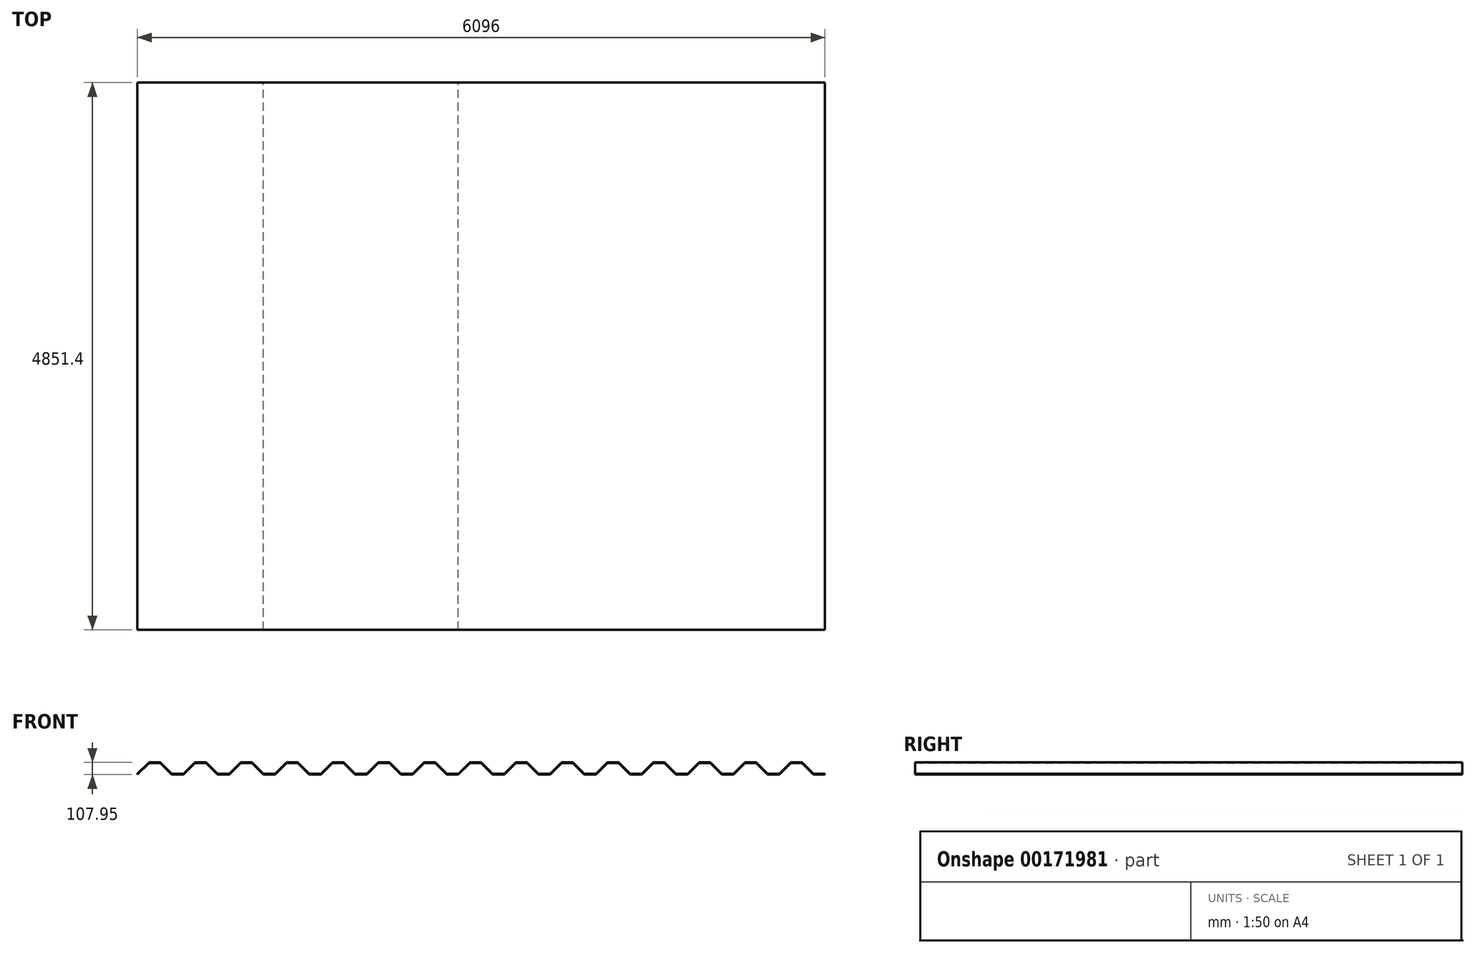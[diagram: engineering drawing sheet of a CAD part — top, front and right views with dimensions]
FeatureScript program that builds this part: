
annotation { "Feature Type Name" : "Feature", "Feature Type Description" : "" }
export const myFeature = defineFeature(function(context is Context, id is Id, definition is map)
    precondition{}
    {
        {
            var Q0;
            Q0=qCreatedBy(makeId("Front.planeOp"),FACE);
            var sketch = newSketch(context, id + "F0", { "sketchPlane" : qUnion([Q0])});
            skLineSegment(sketch, "E0", {"start": v(0, 0) * mm, "end": v(101.6, 101.6) * mm});
            skLineSegment(sketch, "E1", {"start": v(101.6, 101.6) * mm, "end": v(203.2, 101.6) * mm});
            skLineSegment(sketch, "E2", {"start": v(203.2, 101.6) * mm, "end": v(304.8, 0) * mm});
            skLineSegment(sketch, "E3", {"start": v(304.8, 0) * mm, "end": v(406.4, 0) * mm});
            skLineSegment(sketch, "E4.1.0.0", {"start": v(406.4, 0) * mm, "end": v(508, 101.6) * mm});
            skLineSegment(sketch, "E4.1.0.1", {"start": v(508, 101.6) * mm, "end": v(609.6, 101.6) * mm});
            skLineSegment(sketch, "E4.1.0.2", {"start": v(609.6, 101.6) * mm, "end": v(711.2, 0) * mm});
            skLineSegment(sketch, "E4.1.0.3", {"start": v(711.2, 0) * mm, "end": v(812.8, 0) * mm});
            skLineSegment(sketch, "E4.2.0.0", {"start": v(812.8, 0) * mm, "end": v(914.4, 101.6) * mm});
            skLineSegment(sketch, "E4.2.0.1", {"start": v(914.4, 101.6) * mm, "end": v(1016, 101.6) * mm});
            skLineSegment(sketch, "E4.2.0.2", {"start": v(1016, 101.6) * mm, "end": v(1117.6, 0) * mm});
            skLineSegment(sketch, "E4.2.0.3", {"start": v(1117.6, 0) * mm, "end": v(1219.2, 0) * mm});
            skLineSegment(sketch, "E4.3.0.0", {"start": v(1219.2, 0) * mm, "end": v(1320.8, 101.6) * mm});
            skLineSegment(sketch, "E4.3.0.1", {"start": v(1320.8, 101.6) * mm, "end": v(1422.4, 101.6) * mm});
            skLineSegment(sketch, "E4.3.0.2", {"start": v(1422.4, 101.6) * mm, "end": v(1524, 0) * mm});
            skLineSegment(sketch, "E4.3.0.3", {"start": v(1524, 0) * mm, "end": v(1625.6, 0) * mm});
            skLineSegment(sketch, "E4.4.0.0", {"start": v(1625.6, 0) * mm, "end": v(1727.2, 101.6) * mm});
            skLineSegment(sketch, "E4.4.0.1", {"start": v(1727.2, 101.6) * mm, "end": v(1828.8, 101.6) * mm});
            skLineSegment(sketch, "E4.4.0.2", {"start": v(1828.8, 101.6) * mm, "end": v(1930.4, 0) * mm});
            skLineSegment(sketch, "E4.4.0.3", {"start": v(1930.4, 0) * mm, "end": v(2032, 0) * mm});
            skLineSegment(sketch, "E4.5.0.0", {"start": v(2032, 0) * mm, "end": v(2133.6, 101.6) * mm});
            skLineSegment(sketch, "E4.5.0.1", {"start": v(2133.6, 101.6) * mm, "end": v(2235.2, 101.6) * mm});
            skLineSegment(sketch, "E4.5.0.2", {"start": v(2235.2, 101.6) * mm, "end": v(2336.8, 0) * mm});
            skLineSegment(sketch, "E4.5.0.3", {"start": v(2336.8, 0) * mm, "end": v(2438.4, 0) * mm});
            skLineSegment(sketch, "E4.6.0.0", {"start": v(2438.4, 0) * mm, "end": v(2540, 101.6) * mm});
            skLineSegment(sketch, "E4.6.0.1", {"start": v(2540, 101.6) * mm, "end": v(2641.6, 101.6) * mm});
            skLineSegment(sketch, "E4.6.0.2", {"start": v(2641.6, 101.6) * mm, "end": v(2743.2, 0) * mm});
            skLineSegment(sketch, "E4.6.0.3", {"start": v(2743.2, 0) * mm, "end": v(2844.8, 0) * mm});
            skLineSegment(sketch, "E4.7.0.0", {"start": v(2844.8, 0) * mm, "end": v(2946.4, 101.6) * mm});
            skLineSegment(sketch, "E4.7.0.1", {"start": v(2946.4, 101.6) * mm, "end": v(3048, 101.6) * mm});
            skLineSegment(sketch, "E4.7.0.2", {"start": v(3048, 101.6) * mm, "end": v(3149.6, 0) * mm});
            skLineSegment(sketch, "E4.7.0.3", {"start": v(3149.6, 0) * mm, "end": v(3251.2, 0) * mm});
            skLineSegment(sketch, "E4.8.0.0", {"start": v(3251.2, 0) * mm, "end": v(3352.8, 101.6) * mm});
            skLineSegment(sketch, "E4.8.0.1", {"start": v(3352.8, 101.6) * mm, "end": v(3454.4, 101.6) * mm});
            skLineSegment(sketch, "E4.8.0.2", {"start": v(3454.4, 101.6) * mm, "end": v(3556, 0) * mm});
            skLineSegment(sketch, "E4.8.0.3", {"start": v(3556, 0) * mm, "end": v(3657.6, 0) * mm});
            skLineSegment(sketch, "E4.9.0.0", {"start": v(3657.6, 0) * mm, "end": v(3759.2, 101.6) * mm});
            skLineSegment(sketch, "E4.9.0.1", {"start": v(3759.2, 101.6) * mm, "end": v(3860.8, 101.6) * mm});
            skLineSegment(sketch, "E4.9.0.2", {"start": v(3860.8, 101.6) * mm, "end": v(3962.4, 0) * mm});
            skLineSegment(sketch, "E4.9.0.3", {"start": v(3962.4, 0) * mm, "end": v(4064, 0) * mm});
            skLineSegment(sketch, "E4.10.0.0", {"start": v(4064, 0) * mm, "end": v(4165.6, 101.6) * mm});
            skLineSegment(sketch, "E4.10.0.1", {"start": v(4165.6, 101.6) * mm, "end": v(4267.2, 101.6) * mm});
            skLineSegment(sketch, "E4.10.0.2", {"start": v(4267.2, 101.6) * mm, "end": v(4368.8, 0) * mm});
            skLineSegment(sketch, "E4.10.0.3", {"start": v(4368.8, 0) * mm, "end": v(4470.4, 0) * mm});
            skLineSegment(sketch, "E4.11.0.0", {"start": v(4470.4, 0) * mm, "end": v(4572, 101.6) * mm});
            skLineSegment(sketch, "E4.11.0.1", {"start": v(4572, 101.6) * mm, "end": v(4673.6, 101.6) * mm});
            skLineSegment(sketch, "E4.11.0.2", {"start": v(4673.6, 101.6) * mm, "end": v(4775.2, 0) * mm});
            skLineSegment(sketch, "E4.11.0.3", {"start": v(4775.2, 0) * mm, "end": v(4876.8, 0) * mm});
            skLineSegment(sketch, "E4.12.0.0", {"start": v(4876.8, 0) * mm, "end": v(4978.4, 101.6) * mm});
            skLineSegment(sketch, "E4.12.0.1", {"start": v(4978.4, 101.6) * mm, "end": v(5080, 101.6) * mm});
            skLineSegment(sketch, "E4.12.0.2", {"start": v(5080, 101.6) * mm, "end": v(5181.6, 0) * mm});
            skLineSegment(sketch, "E4.12.0.3", {"start": v(5181.6, 0) * mm, "end": v(5283.2, 0) * mm});
            skLineSegment(sketch, "E4.13.0.0", {"start": v(5283.2, 0) * mm, "end": v(5384.8, 101.6) * mm});
            skLineSegment(sketch, "E4.13.0.1", {"start": v(5384.8, 101.6) * mm, "end": v(5486.4, 101.6) * mm});
            skLineSegment(sketch, "E4.13.0.2", {"start": v(5486.4, 101.6) * mm, "end": v(5588, 0) * mm});
            skLineSegment(sketch, "E4.13.0.3", {"start": v(5588, 0) * mm, "end": v(5689.6, 0) * mm});
            skLineSegment(sketch, "E4.14.0.0", {"start": v(5689.6, 0) * mm, "end": v(5791.2, 101.6) * mm});
            skLineSegment(sketch, "E4.14.0.1", {"start": v(5791.2, 101.6) * mm, "end": v(5892.8, 101.6) * mm});
            skLineSegment(sketch, "E4.14.0.2", {"start": v(5892.8, 101.6) * mm, "end": v(5994.4, 0) * mm});
            skLineSegment(sketch, "E4.14.0.3", {"start": v(5994.4, 0) * mm, "end": v(6096, 0) * mm});
            skLineSegment(sketch, "E5.0.1.0", {"start": v(5994.4, 6.35) * mm, "end": v(6096, 6.35) * mm});
            skLineSegment(sketch, "E5.0.1.1", {"start": v(0, 6.35) * mm, "end": v(101.6, 107.95) * mm});
            skLineSegment(sketch, "E5.0.1.2", {"start": v(5486.4, 107.95) * mm, "end": v(5588, 6.35) * mm});
            skLineSegment(sketch, "E5.0.1.3", {"start": v(5080, 107.95) * mm, "end": v(5181.6, 6.35) * mm});
            skLineSegment(sketch, "E5.0.1.4", {"start": v(2235.2, 107.95) * mm, "end": v(2336.8, 6.35) * mm});
            skLineSegment(sketch, "E5.0.1.5", {"start": v(3454.4, 107.95) * mm, "end": v(3556, 6.35) * mm});
            skLineSegment(sketch, "E5.0.1.6", {"start": v(3860.8, 107.95) * mm, "end": v(3962.4, 6.35) * mm});
            skLineSegment(sketch, "E5.0.1.7", {"start": v(1828.8, 107.95) * mm, "end": v(1930.4, 6.35) * mm});
            skLineSegment(sketch, "E5.0.1.8", {"start": v(3149.6, 6.35) * mm, "end": v(3251.2, 6.35) * mm});
            skLineSegment(sketch, "E5.0.1.9", {"start": v(4775.2, 6.35) * mm, "end": v(4876.8, 6.35) * mm});
            skLineSegment(sketch, "E5.0.1.10", {"start": v(2540, 107.95) * mm, "end": v(2641.6, 107.95) * mm});
            skLineSegment(sketch, "E5.0.1.11", {"start": v(4165.6, 107.95) * mm, "end": v(4267.2, 107.95) * mm});
            skLineSegment(sketch, "E5.0.1.12", {"start": v(5791.2, 107.95) * mm, "end": v(5892.8, 107.95) * mm});
            skLineSegment(sketch, "E5.0.1.13", {"start": v(4978.4, 107.95) * mm, "end": v(5080, 107.95) * mm});
            skLineSegment(sketch, "E5.0.1.14", {"start": v(3352.8, 107.95) * mm, "end": v(3454.4, 107.95) * mm});
            skLineSegment(sketch, "E5.0.1.15", {"start": v(1727.2, 107.95) * mm, "end": v(1828.8, 107.95) * mm});
            skLineSegment(sketch, "E5.0.1.16", {"start": v(3759.2, 107.95) * mm, "end": v(3860.8, 107.95) * mm});
            skLineSegment(sketch, "E5.0.1.17", {"start": v(3048, 107.95) * mm, "end": v(3149.6, 6.35) * mm});
            skLineSegment(sketch, "E5.0.1.18", {"start": v(4673.6, 107.95) * mm, "end": v(4775.2, 6.35) * mm});
            skLineSegment(sketch, "E5.0.1.19", {"start": v(5384.8, 107.95) * mm, "end": v(5486.4, 107.95) * mm});
            skLineSegment(sketch, "E5.0.1.20", {"start": v(2133.6, 107.95) * mm, "end": v(2235.2, 107.95) * mm});
            skLineSegment(sketch, "E5.0.1.21", {"start": v(2438.4, 6.35) * mm, "end": v(2540, 107.95) * mm});
            skLineSegment(sketch, "E5.0.1.22", {"start": v(4064, 6.35) * mm, "end": v(4165.6, 107.95) * mm});
            skLineSegment(sketch, "E5.0.1.23", {"start": v(5689.6, 6.35) * mm, "end": v(5791.2, 107.95) * mm});
            skLineSegment(sketch, "E5.0.1.24", {"start": v(2844.8, 6.35) * mm, "end": v(2946.4, 107.95) * mm});
            skLineSegment(sketch, "E5.0.1.25", {"start": v(4470.4, 6.35) * mm, "end": v(4572, 107.95) * mm});
            skLineSegment(sketch, "E5.0.1.26", {"start": v(3251.2, 6.35) * mm, "end": v(3352.8, 107.95) * mm});
            skLineSegment(sketch, "E5.0.1.27", {"start": v(4876.8, 6.35) * mm, "end": v(4978.4, 107.95) * mm});
            skLineSegment(sketch, "E5.0.1.28", {"start": v(1625.6, 6.35) * mm, "end": v(1727.2, 107.95) * mm});
            skLineSegment(sketch, "E5.0.1.29", {"start": v(3657.6, 6.35) * mm, "end": v(3759.2, 107.95) * mm});
            skLineSegment(sketch, "E5.0.1.30", {"start": v(4572, 107.95) * mm, "end": v(4673.6, 107.95) * mm});
            skLineSegment(sketch, "E5.0.1.31", {"start": v(2946.4, 107.95) * mm, "end": v(3048, 107.95) * mm});
            skLineSegment(sketch, "E5.0.1.32", {"start": v(5283.2, 6.35) * mm, "end": v(5384.8, 107.95) * mm});
            skLineSegment(sketch, "E5.0.1.33", {"start": v(2032, 6.35) * mm, "end": v(2133.6, 107.95) * mm});
            skLineSegment(sketch, "E5.0.1.34", {"start": v(2336.8, 6.35) * mm, "end": v(2438.4, 6.35) * mm});
            skLineSegment(sketch, "E5.0.1.35", {"start": v(3962.4, 6.35) * mm, "end": v(4064, 6.35) * mm});
            skLineSegment(sketch, "E5.0.1.36", {"start": v(5588, 6.35) * mm, "end": v(5689.6, 6.35) * mm});
            skLineSegment(sketch, "E5.0.1.37", {"start": v(2743.2, 6.35) * mm, "end": v(2844.8, 6.35) * mm});
            skLineSegment(sketch, "E5.0.1.38", {"start": v(4368.8, 6.35) * mm, "end": v(4470.4, 6.35) * mm});
            skLineSegment(sketch, "E5.0.1.39", {"start": v(1219.2, 6.35) * mm, "end": v(1320.8, 107.95) * mm});
            skLineSegment(sketch, "E5.0.1.40", {"start": v(1117.6, 6.35) * mm, "end": v(1219.2, 6.35) * mm});
            skLineSegment(sketch, "E5.0.1.41", {"start": v(1016, 107.95) * mm, "end": v(1117.6, 6.35) * mm});
            skLineSegment(sketch, "E5.0.1.42", {"start": v(914.4, 107.95) * mm, "end": v(1016, 107.95) * mm});
            skLineSegment(sketch, "E5.0.1.43", {"start": v(812.8, 6.35) * mm, "end": v(914.4, 107.95) * mm});
            skLineSegment(sketch, "E5.0.1.44", {"start": v(711.2, 6.35) * mm, "end": v(812.8, 6.35) * mm});
            skLineSegment(sketch, "E5.0.1.45", {"start": v(609.6, 107.95) * mm, "end": v(711.2, 6.35) * mm});
            skLineSegment(sketch, "E5.0.1.46", {"start": v(508, 107.95) * mm, "end": v(609.6, 107.95) * mm});
            skLineSegment(sketch, "E5.0.1.47", {"start": v(406.4, 6.35) * mm, "end": v(508, 107.95) * mm});
            skLineSegment(sketch, "E5.0.1.48", {"start": v(304.8, 6.35) * mm, "end": v(406.4, 6.35) * mm});
            skLineSegment(sketch, "E5.0.1.49", {"start": v(203.2, 107.95) * mm, "end": v(304.8, 6.35) * mm});
            skLineSegment(sketch, "E5.0.1.50", {"start": v(101.6, 107.95) * mm, "end": v(203.2, 107.95) * mm});
            skLineSegment(sketch, "E5.0.1.51", {"start": v(1524, 6.35) * mm, "end": v(1625.6, 6.35) * mm});
            skLineSegment(sketch, "E5.0.1.52", {"start": v(1422.4, 107.95) * mm, "end": v(1524, 6.35) * mm});
            skLineSegment(sketch, "E5.0.1.53", {"start": v(1320.8, 107.95) * mm, "end": v(1422.4, 107.95) * mm});
            skLineSegment(sketch, "E5.0.1.54", {"start": v(3556, 6.35) * mm, "end": v(3657.6, 6.35) * mm});
            skLineSegment(sketch, "E5.0.1.55", {"start": v(5181.6, 6.35) * mm, "end": v(5283.2, 6.35) * mm});
            skLineSegment(sketch, "E5.0.1.56", {"start": v(1930.4, 6.35) * mm, "end": v(2032, 6.35) * mm});
            skLineSegment(sketch, "E5.0.1.57", {"start": v(2641.6, 107.95) * mm, "end": v(2743.2, 6.35) * mm});
            skLineSegment(sketch, "E5.0.1.58", {"start": v(4267.2, 107.95) * mm, "end": v(4368.8, 6.35) * mm});
            skLineSegment(sketch, "E5.0.1.59", {"start": v(5892.8, 107.95) * mm, "end": v(5994.4, 6.35) * mm});
            skLineSegment(sketch, "E5.direction2", {"start": v(0, 0) * mm, "end": v(0, 6.35) * mm, "construction": true});
            skLineSegment(sketch, "E6", {"start": v(0, 6.35) * mm, "end": v(0, 0) * mm});
            skLineSegment(sketch, "E7", {"start": v(6096, 6.35) * mm, "end": v(6096, 0) * mm});
            skSolve(sketch);
        }
        {
            var Q0;
            Q0 = qSketchRegion(id + "F0", true);
            extrude(context, id + "F1", {"entities" : qUnion([Q0]), "depth" : 4851.4 * mm});
        }
        {
            var Q0;
            Q0=makeQuery(id+"F1.opExtrude","SWEPT_EDGE",EDGE,{"disambiguationData":[OSD([sQuery(id+"F0.wireOp",EDGE,"E5.0.1.1"),sQuery(id+"F0.wireOp",EDGE,"E5.0.1.50")])]});
            var Q1;
            Q1=makeQuery(id+"F1.opExtrude","SWEPT_EDGE",EDGE,{"disambiguationData":[OSD([sQuery(id+"F0.wireOp",EDGE,"E5.0.1.49"),sQuery(id+"F0.wireOp",EDGE,"E5.0.1.50")])]});
            var Q2;
            Q2=makeQuery(id+"F1.opExtrude","SWEPT_EDGE",EDGE,{"disambiguationData":[OSD([sQuery(id+"F0.wireOp",EDGE,"E5.0.1.48"),sQuery(id+"F0.wireOp",EDGE,"E5.0.1.49")])]});
            var Q3;
            Q3=makeQuery(id+"F1.opExtrude","SWEPT_EDGE",EDGE,{"disambiguationData":[OSD([sQuery(id+"F0.wireOp",EDGE,"E5.0.1.47"),sQuery(id+"F0.wireOp",EDGE,"E5.0.1.48")])]});
            var Q4;
            Q4=makeQuery(id+"F1.opExtrude","SWEPT_EDGE",EDGE,{"disambiguationData":[OSD([sQuery(id+"F0.wireOp",EDGE,"E5.0.1.46"),sQuery(id+"F0.wireOp",EDGE,"E5.0.1.47")])]});
            var Q5;
            Q5=makeQuery(id+"F1.opExtrude","SWEPT_EDGE",EDGE,{"disambiguationData":[OSD([sQuery(id+"F0.wireOp",EDGE,"E5.0.1.45"),sQuery(id+"F0.wireOp",EDGE,"E5.0.1.46")])]});
            var Q6;
            Q6=makeQuery(id+"F1.opExtrude","SWEPT_EDGE",EDGE,{"disambiguationData":[OSD([sQuery(id+"F0.wireOp",EDGE,"E5.0.1.44"),sQuery(id+"F0.wireOp",EDGE,"E5.0.1.45")])]});
            var Q7;
            Q7=makeQuery(id+"F1.opExtrude","SWEPT_EDGE",EDGE,{"disambiguationData":[OSD([sQuery(id+"F0.wireOp",EDGE,"E5.0.1.43"),sQuery(id+"F0.wireOp",EDGE,"E5.0.1.44")])]});
            var Q8;
            Q8=makeQuery(id+"F1.opExtrude","SWEPT_EDGE",EDGE,{"disambiguationData":[OSD([sQuery(id+"F0.wireOp",EDGE,"E5.0.1.42"),sQuery(id+"F0.wireOp",EDGE,"E5.0.1.43")])]});
            var Q9;
            Q9=makeQuery(id+"F1.opExtrude","SWEPT_EDGE",EDGE,{"disambiguationData":[OSD([sQuery(id+"F0.wireOp",EDGE,"E5.0.1.41"),sQuery(id+"F0.wireOp",EDGE,"E5.0.1.42")])]});
            var Q10;
            Q10=makeQuery(id+"F1.opExtrude","SWEPT_EDGE",EDGE,{"disambiguationData":[OSD([sQuery(id+"F0.wireOp",EDGE,"E5.0.1.40"),sQuery(id+"F0.wireOp",EDGE,"E5.0.1.41")])]});
            var Q11;
            Q11=makeQuery(id+"F1.opExtrude","SWEPT_EDGE",EDGE,{"disambiguationData":[OSD([sQuery(id+"F0.wireOp",EDGE,"E5.0.1.39"),sQuery(id+"F0.wireOp",EDGE,"E5.0.1.40")])]});
            var Q12;
            Q12=makeQuery(id+"F1.opExtrude","SWEPT_EDGE",EDGE,{"disambiguationData":[OSD([sQuery(id+"F0.wireOp",EDGE,"E5.0.1.39"),sQuery(id+"F0.wireOp",EDGE,"E5.0.1.53")])]});
            var Q13;
            Q13=makeQuery(id+"F1.opExtrude","SWEPT_EDGE",EDGE,{"disambiguationData":[OSD([sQuery(id+"F0.wireOp",EDGE,"E5.0.1.52"),sQuery(id+"F0.wireOp",EDGE,"E5.0.1.53")])]});
            var Q14;
            Q14=makeQuery(id+"F1.opExtrude","SWEPT_EDGE",EDGE,{"disambiguationData":[OSD([sQuery(id+"F0.wireOp",EDGE,"E5.0.1.51"),sQuery(id+"F0.wireOp",EDGE,"E5.0.1.52")])]});
            var Q15;
            Q15=makeQuery(id+"F1.opExtrude","SWEPT_EDGE",EDGE,{"disambiguationData":[OSD([sQuery(id+"F0.wireOp",EDGE,"E5.0.1.28"),sQuery(id+"F0.wireOp",EDGE,"E5.0.1.51")])]});
            var Q16;
            Q16=makeQuery(id+"F1.opExtrude","SWEPT_EDGE",EDGE,{"disambiguationData":[OSD([sQuery(id+"F0.wireOp",EDGE,"E5.0.1.15"),sQuery(id+"F0.wireOp",EDGE,"E5.0.1.28")])]});
            var Q17;
            Q17=makeQuery(id+"F1.opExtrude","SWEPT_EDGE",EDGE,{"disambiguationData":[OSD([sQuery(id+"F0.wireOp",EDGE,"E5.0.1.7"),sQuery(id+"F0.wireOp",EDGE,"E5.0.1.15")])]});
            var Q18;
            Q18=makeQuery(id+"F1.opExtrude","SWEPT_EDGE",EDGE,{"disambiguationData":[OSD([sQuery(id+"F0.wireOp",EDGE,"E5.0.1.7"),sQuery(id+"F0.wireOp",EDGE,"E5.0.1.56")])]});
            var Q19;
            Q19=makeQuery(id+"F1.opExtrude","SWEPT_EDGE",EDGE,{"disambiguationData":[OSD([sQuery(id+"F0.wireOp",EDGE,"E5.0.1.33"),sQuery(id+"F0.wireOp",EDGE,"E5.0.1.56")])]});
            var Q20;
            Q20=makeQuery(id+"F1.opExtrude","SWEPT_EDGE",EDGE,{"disambiguationData":[OSD([sQuery(id+"F0.wireOp",EDGE,"E5.0.1.20"),sQuery(id+"F0.wireOp",EDGE,"E5.0.1.33")])]});
            var Q21;
            Q21=makeQuery(id+"F1.opExtrude","SWEPT_EDGE",EDGE,{"disambiguationData":[OSD([sQuery(id+"F0.wireOp",EDGE,"E5.0.1.4"),sQuery(id+"F0.wireOp",EDGE,"E5.0.1.20")])]});
            var Q22;
            Q22=makeQuery(id+"F1.opExtrude","SWEPT_EDGE",EDGE,{"disambiguationData":[OSD([sQuery(id+"F0.wireOp",EDGE,"E5.0.1.4"),sQuery(id+"F0.wireOp",EDGE,"E5.0.1.34")])]});
            var Q23;
            Q23=makeQuery(id+"F1.opExtrude","SWEPT_EDGE",EDGE,{"disambiguationData":[OSD([sQuery(id+"F0.wireOp",EDGE,"E5.0.1.21"),sQuery(id+"F0.wireOp",EDGE,"E5.0.1.34")])]});
            var Q24;
            Q24=makeQuery(id+"F1.opExtrude","SWEPT_EDGE",EDGE,{"disambiguationData":[OSD([sQuery(id+"F0.wireOp",EDGE,"E5.0.1.10"),sQuery(id+"F0.wireOp",EDGE,"E5.0.1.21")])]});
            var Q25;
            Q25=makeQuery(id+"F1.opExtrude","SWEPT_EDGE",EDGE,{"disambiguationData":[OSD([sQuery(id+"F0.wireOp",EDGE,"E5.0.1.10"),sQuery(id+"F0.wireOp",EDGE,"E5.0.1.57")])]});
            var Q26;
            Q26=makeQuery(id+"F1.opExtrude","SWEPT_EDGE",EDGE,{"disambiguationData":[OSD([sQuery(id+"F0.wireOp",EDGE,"E5.0.1.37"),sQuery(id+"F0.wireOp",EDGE,"E5.0.1.57")])]});
            var Q27;
            Q27=makeQuery(id+"F1.opExtrude","SWEPT_EDGE",EDGE,{"disambiguationData":[OSD([sQuery(id+"F0.wireOp",EDGE,"E5.0.1.24"),sQuery(id+"F0.wireOp",EDGE,"E5.0.1.37")])]});
            var Q28;
            Q28=makeQuery(id+"F1.opExtrude","SWEPT_EDGE",EDGE,{"disambiguationData":[OSD([sQuery(id+"F0.wireOp",EDGE,"E5.0.1.24"),sQuery(id+"F0.wireOp",EDGE,"E5.0.1.31")])]});
            var Q29;
            Q29=makeQuery(id+"F1.opExtrude","SWEPT_EDGE",EDGE,{"disambiguationData":[OSD([sQuery(id+"F0.wireOp",EDGE,"E5.0.1.17"),sQuery(id+"F0.wireOp",EDGE,"E5.0.1.31")])]});
            var Q30;
            Q30=makeQuery(id+"F1.opExtrude","SWEPT_EDGE",EDGE,{"disambiguationData":[OSD([sQuery(id+"F0.wireOp",EDGE,"E5.0.1.8"),sQuery(id+"F0.wireOp",EDGE,"E5.0.1.17")])]});
            var Q31;
            Q31=makeQuery(id+"F1.opExtrude","SWEPT_EDGE",EDGE,{"disambiguationData":[OSD([sQuery(id+"F0.wireOp",EDGE,"E5.0.1.8"),sQuery(id+"F0.wireOp",EDGE,"E5.0.1.26")])]});
            var Q32;
            Q32=makeQuery(id+"F1.opExtrude","SWEPT_EDGE",EDGE,{"disambiguationData":[OSD([sQuery(id+"F0.wireOp",EDGE,"E5.0.1.14"),sQuery(id+"F0.wireOp",EDGE,"E5.0.1.26")])]});
            var Q33;
            Q33=makeQuery(id+"F1.opExtrude","SWEPT_EDGE",EDGE,{"disambiguationData":[OSD([sQuery(id+"F0.wireOp",EDGE,"E5.0.1.5"),sQuery(id+"F0.wireOp",EDGE,"E5.0.1.14")])]});
            var Q34;
            Q34=makeQuery(id+"F1.opExtrude","SWEPT_EDGE",EDGE,{"disambiguationData":[OSD([sQuery(id+"F0.wireOp",EDGE,"E5.0.1.5"),sQuery(id+"F0.wireOp",EDGE,"E5.0.1.54")])]});
            var Q35;
            Q35=makeQuery(id+"F1.opExtrude","SWEPT_EDGE",EDGE,{"disambiguationData":[OSD([sQuery(id+"F0.wireOp",EDGE,"E5.0.1.29"),sQuery(id+"F0.wireOp",EDGE,"E5.0.1.54")])]});
            var Q36;
            Q36=makeQuery(id+"F1.opExtrude","SWEPT_EDGE",EDGE,{"disambiguationData":[OSD([sQuery(id+"F0.wireOp",EDGE,"E5.0.1.16"),sQuery(id+"F0.wireOp",EDGE,"E5.0.1.29")])]});
            var Q37;
            Q37=makeQuery(id+"F1.opExtrude","SWEPT_EDGE",EDGE,{"disambiguationData":[OSD([sQuery(id+"F0.wireOp",EDGE,"E5.0.1.6"),sQuery(id+"F0.wireOp",EDGE,"E5.0.1.16")])]});
            var Q38;
            Q38=makeQuery(id+"F1.opExtrude","SWEPT_EDGE",EDGE,{"disambiguationData":[OSD([sQuery(id+"F0.wireOp",EDGE,"E5.0.1.6"),sQuery(id+"F0.wireOp",EDGE,"E5.0.1.35")])]});
            var Q39;
            Q39=makeQuery(id+"F1.opExtrude","SWEPT_EDGE",EDGE,{"disambiguationData":[OSD([sQuery(id+"F0.wireOp",EDGE,"E5.0.1.22"),sQuery(id+"F0.wireOp",EDGE,"E5.0.1.35")])]});
            var Q40;
            Q40=makeQuery(id+"F1.opExtrude","SWEPT_EDGE",EDGE,{"disambiguationData":[OSD([sQuery(id+"F0.wireOp",EDGE,"E5.0.1.11"),sQuery(id+"F0.wireOp",EDGE,"E5.0.1.22")])]});
            var Q41;
            Q41=makeQuery(id+"F1.opExtrude","SWEPT_EDGE",EDGE,{"disambiguationData":[OSD([sQuery(id+"F0.wireOp",EDGE,"E5.0.1.11"),sQuery(id+"F0.wireOp",EDGE,"E5.0.1.58")])]});
            var Q42;
            Q42=makeQuery(id+"F1.opExtrude","SWEPT_EDGE",EDGE,{"disambiguationData":[OSD([sQuery(id+"F0.wireOp",EDGE,"E5.0.1.38"),sQuery(id+"F0.wireOp",EDGE,"E5.0.1.58")])]});
            var Q43;
            Q43=makeQuery(id+"F1.opExtrude","SWEPT_EDGE",EDGE,{"disambiguationData":[OSD([sQuery(id+"F0.wireOp",EDGE,"E5.0.1.25"),sQuery(id+"F0.wireOp",EDGE,"E5.0.1.38")])]});
            var Q44;
            Q44=makeQuery(id+"F1.opExtrude","SWEPT_EDGE",EDGE,{"disambiguationData":[OSD([sQuery(id+"F0.wireOp",EDGE,"E5.0.1.25"),sQuery(id+"F0.wireOp",EDGE,"E5.0.1.30")])]});
            var Q45;
            Q45=makeQuery(id+"F1.opExtrude","SWEPT_EDGE",EDGE,{"disambiguationData":[OSD([sQuery(id+"F0.wireOp",EDGE,"E5.0.1.18"),sQuery(id+"F0.wireOp",EDGE,"E5.0.1.30")])]});
            var Q46;
            Q46=makeQuery(id+"F1.opExtrude","SWEPT_EDGE",EDGE,{"disambiguationData":[OSD([sQuery(id+"F0.wireOp",EDGE,"E5.0.1.9"),sQuery(id+"F0.wireOp",EDGE,"E5.0.1.18")])]});
            var Q47;
            Q47=makeQuery(id+"F1.opExtrude","SWEPT_EDGE",EDGE,{"disambiguationData":[OSD([sQuery(id+"F0.wireOp",EDGE,"E5.0.1.9"),sQuery(id+"F0.wireOp",EDGE,"E5.0.1.27")])]});
            var Q48;
            Q48=makeQuery(id+"F1.opExtrude","SWEPT_EDGE",EDGE,{"disambiguationData":[OSD([sQuery(id+"F0.wireOp",EDGE,"E5.0.1.13"),sQuery(id+"F0.wireOp",EDGE,"E5.0.1.27")])]});
            var Q49;
            Q49=makeQuery(id+"F1.opExtrude","SWEPT_EDGE",EDGE,{"disambiguationData":[OSD([sQuery(id+"F0.wireOp",EDGE,"E5.0.1.3"),sQuery(id+"F0.wireOp",EDGE,"E5.0.1.13")])]});
            var Q50;
            Q50=makeQuery(id+"F1.opExtrude","SWEPT_EDGE",EDGE,{"disambiguationData":[OSD([sQuery(id+"F0.wireOp",EDGE,"E5.0.1.3"),sQuery(id+"F0.wireOp",EDGE,"E5.0.1.55")])]});
            var Q51;
            Q51=makeQuery(id+"F1.opExtrude","SWEPT_EDGE",EDGE,{"disambiguationData":[OSD([sQuery(id+"F0.wireOp",EDGE,"E5.0.1.32"),sQuery(id+"F0.wireOp",EDGE,"E5.0.1.55")])]});
            var Q52;
            Q52=makeQuery(id+"F1.opExtrude","SWEPT_EDGE",EDGE,{"disambiguationData":[OSD([sQuery(id+"F0.wireOp",EDGE,"E5.0.1.19"),sQuery(id+"F0.wireOp",EDGE,"E5.0.1.32")])]});
            var Q53;
            Q53=makeQuery(id+"F1.opExtrude","SWEPT_EDGE",EDGE,{"disambiguationData":[OSD([sQuery(id+"F0.wireOp",EDGE,"E5.0.1.2"),sQuery(id+"F0.wireOp",EDGE,"E5.0.1.19")])]});
            var Q54;
            Q54=makeQuery(id+"F1.opExtrude","SWEPT_EDGE",EDGE,{"disambiguationData":[OSD([sQuery(id+"F0.wireOp",EDGE,"E5.0.1.2"),sQuery(id+"F0.wireOp",EDGE,"E5.0.1.36")])]});
            var Q55;
            Q55=makeQuery(id+"F1.opExtrude","SWEPT_EDGE",EDGE,{"disambiguationData":[OSD([sQuery(id+"F0.wireOp",EDGE,"E5.0.1.23"),sQuery(id+"F0.wireOp",EDGE,"E5.0.1.36")])]});
            var Q56;
            Q56=makeQuery(id+"F1.opExtrude","SWEPT_EDGE",EDGE,{"disambiguationData":[OSD([sQuery(id+"F0.wireOp",EDGE,"E5.0.1.12"),sQuery(id+"F0.wireOp",EDGE,"E5.0.1.23")])]});
            var Q57;
            Q57=makeQuery(id+"F1.opExtrude","SWEPT_EDGE",EDGE,{"disambiguationData":[OSD([sQuery(id+"F0.wireOp",EDGE,"E5.0.1.12"),sQuery(id+"F0.wireOp",EDGE,"E5.0.1.59")])]});
            var Q58;
            Q58=makeQuery(id+"F1.opExtrude","SWEPT_EDGE",EDGE,{"disambiguationData":[OSD([sQuery(id+"F0.wireOp",EDGE,"E5.0.1.0"),sQuery(id+"F0.wireOp",EDGE,"E5.0.1.59")])]});
            fillet(context, id + "F2", {"entities" : qUnion([Q0, Q1, Q2, Q3, Q4, Q5, Q6, Q7, Q8, Q9, Q10, Q11, Q12, Q13, Q14, Q15, Q16, Q17, Q18, Q19, Q20, Q21, Q22, Q23, Q24, Q25, Q26, Q27, Q28, Q29, Q30, Q31, Q32, Q33, Q34, Q35, Q36, Q37, Q38, Q39, Q40, Q41, Q42, Q43, Q44, Q45, Q46, Q47, Q48, Q49, Q50, Q51, Q52, Q53, Q54, Q55, Q56, Q57, Q58]), "radius" : 12.7 * mm, "tangentPropagation" : true, "allowEdgeOverflow" : false});
        }
        {
            var Q0;
            Q0=makeQuery(id+"F1.opExtrude","SWEPT_EDGE",EDGE,{"disambiguationData":[OSD([sQuery(id+"F0.wireOp",EDGE,"E0"),sQuery(id+"F0.wireOp",EDGE,"E1")])]});
            var Q1;
            Q1=makeQuery(id+"F1.opExtrude","SWEPT_EDGE",EDGE,{"disambiguationData":[OSD([sQuery(id+"F0.wireOp",EDGE,"E1"),sQuery(id+"F0.wireOp",EDGE,"E2")])]});
            var Q2;
            Q2=makeQuery(id+"F1.opExtrude","SWEPT_EDGE",EDGE,{"disambiguationData":[OSD([sQuery(id+"F0.wireOp",EDGE,"E2"),sQuery(id+"F0.wireOp",EDGE,"E3")])]});
            var Q3;
            Q3=makeQuery(id+"F1.opExtrude","SWEPT_EDGE",EDGE,{"disambiguationData":[OSD([sQuery(id+"F0.wireOp",EDGE,"E3"),sQuery(id+"F0.wireOp",EDGE,"E4.1.0.0")])]});
            var Q4;
            Q4=makeQuery(id+"F1.opExtrude","SWEPT_EDGE",EDGE,{"disambiguationData":[OSD([sQuery(id+"F0.wireOp",EDGE,"E4.1.0.0"),sQuery(id+"F0.wireOp",EDGE,"E4.1.0.1")])]});
            var Q5;
            Q5=makeQuery(id+"F1.opExtrude","SWEPT_EDGE",EDGE,{"disambiguationData":[OSD([sQuery(id+"F0.wireOp",EDGE,"E4.1.0.1"),sQuery(id+"F0.wireOp",EDGE,"E4.1.0.2")])]});
            var Q6;
            Q6=makeQuery(id+"F1.opExtrude","SWEPT_EDGE",EDGE,{"disambiguationData":[OSD([sQuery(id+"F0.wireOp",EDGE,"E4.1.0.2"),sQuery(id+"F0.wireOp",EDGE,"E4.1.0.3")])]});
            var Q7;
            Q7=makeQuery(id+"F1.opExtrude","SWEPT_EDGE",EDGE,{"disambiguationData":[OSD([sQuery(id+"F0.wireOp",EDGE,"E4.1.0.3"),sQuery(id+"F0.wireOp",EDGE,"E4.2.0.0")])]});
            var Q8;
            Q8=makeQuery(id+"F1.opExtrude","SWEPT_EDGE",EDGE,{"disambiguationData":[OSD([sQuery(id+"F0.wireOp",EDGE,"E4.2.0.0"),sQuery(id+"F0.wireOp",EDGE,"E4.2.0.1")])]});
            var Q9;
            Q9=makeQuery(id+"F1.opExtrude","SWEPT_EDGE",EDGE,{"disambiguationData":[OSD([sQuery(id+"F0.wireOp",EDGE,"E4.2.0.1"),sQuery(id+"F0.wireOp",EDGE,"E4.2.0.2")])]});
            var Q10;
            Q10=makeQuery(id+"F1.opExtrude","SWEPT_EDGE",EDGE,{"disambiguationData":[OSD([sQuery(id+"F0.wireOp",EDGE,"E4.2.0.3"),sQuery(id+"F0.wireOp",EDGE,"E4.3.0.0")])]});
            var Q11;
            Q11=makeQuery(id+"F1.opExtrude","SWEPT_EDGE",EDGE,{"disambiguationData":[OSD([sQuery(id+"F0.wireOp",EDGE,"E4.3.0.0"),sQuery(id+"F0.wireOp",EDGE,"E4.3.0.1")])]});
            var Q12;
            Q12=makeQuery(id+"F1.opExtrude","SWEPT_EDGE",EDGE,{"disambiguationData":[OSD([sQuery(id+"F0.wireOp",EDGE,"E4.3.0.1"),sQuery(id+"F0.wireOp",EDGE,"E4.3.0.2")])]});
            var Q13;
            Q13=makeQuery(id+"F1.opExtrude","SWEPT_EDGE",EDGE,{"disambiguationData":[OSD([sQuery(id+"F0.wireOp",EDGE,"E4.3.0.2"),sQuery(id+"F0.wireOp",EDGE,"E4.3.0.3")])]});
            var Q14;
            Q14=makeQuery(id+"F1.opExtrude","SWEPT_EDGE",EDGE,{"disambiguationData":[OSD([sQuery(id+"F0.wireOp",EDGE,"E4.3.0.3"),sQuery(id+"F0.wireOp",EDGE,"E4.4.0.0")])]});
            var Q15;
            Q15=makeQuery(id+"F1.opExtrude","SWEPT_EDGE",EDGE,{"disambiguationData":[OSD([sQuery(id+"F0.wireOp",EDGE,"E4.4.0.0"),sQuery(id+"F0.wireOp",EDGE,"E4.4.0.1")])]});
            var Q16;
            Q16=makeQuery(id+"F1.opExtrude","SWEPT_EDGE",EDGE,{"disambiguationData":[OSD([sQuery(id+"F0.wireOp",EDGE,"E4.4.0.1"),sQuery(id+"F0.wireOp",EDGE,"E4.4.0.2")])]});
            var Q17;
            Q17=makeQuery(id+"F1.opExtrude","SWEPT_EDGE",EDGE,{"disambiguationData":[OSD([sQuery(id+"F0.wireOp",EDGE,"E4.4.0.2"),sQuery(id+"F0.wireOp",EDGE,"E4.4.0.3")])]});
            var Q18;
            Q18=makeQuery(id+"F1.opExtrude","SWEPT_EDGE",EDGE,{"disambiguationData":[OSD([sQuery(id+"F0.wireOp",EDGE,"E4.4.0.3"),sQuery(id+"F0.wireOp",EDGE,"E4.5.0.0")])]});
            var Q19;
            Q19=makeQuery(id+"F1.opExtrude","SWEPT_EDGE",EDGE,{"disambiguationData":[OSD([sQuery(id+"F0.wireOp",EDGE,"E4.5.0.0"),sQuery(id+"F0.wireOp",EDGE,"E4.5.0.1")])]});
            var Q20;
            Q20=makeQuery(id+"F1.opExtrude","SWEPT_EDGE",EDGE,{"disambiguationData":[OSD([sQuery(id+"F0.wireOp",EDGE,"E4.5.0.1"),sQuery(id+"F0.wireOp",EDGE,"E4.5.0.2")])]});
            var Q21;
            Q21=makeQuery(id+"F1.opExtrude","SWEPT_EDGE",EDGE,{"disambiguationData":[OSD([sQuery(id+"F0.wireOp",EDGE,"E4.5.0.2"),sQuery(id+"F0.wireOp",EDGE,"E4.5.0.3")])]});
            var Q22;
            Q22=makeQuery(id+"F1.opExtrude","SWEPT_EDGE",EDGE,{"disambiguationData":[OSD([sQuery(id+"F0.wireOp",EDGE,"E4.5.0.3"),sQuery(id+"F0.wireOp",EDGE,"E4.6.0.0")])]});
            var Q23;
            Q23=makeQuery(id+"F1.opExtrude","SWEPT_EDGE",EDGE,{"disambiguationData":[OSD([sQuery(id+"F0.wireOp",EDGE,"E4.6.0.1"),sQuery(id+"F0.wireOp",EDGE,"E4.6.0.2")])]});
            var Q24;
            Q24=makeQuery(id+"F1.opExtrude","SWEPT_EDGE",EDGE,{"disambiguationData":[OSD([sQuery(id+"F0.wireOp",EDGE,"E4.6.0.0"),sQuery(id+"F0.wireOp",EDGE,"E4.6.0.1")])]});
            var Q25;
            Q25=makeQuery(id+"F1.opExtrude","SWEPT_EDGE",EDGE,{"disambiguationData":[OSD([sQuery(id+"F0.wireOp",EDGE,"E4.6.0.2"),sQuery(id+"F0.wireOp",EDGE,"E4.6.0.3")])]});
            var Q26;
            Q26=makeQuery(id+"F1.opExtrude","SWEPT_EDGE",EDGE,{"disambiguationData":[OSD([sQuery(id+"F0.wireOp",EDGE,"E4.7.0.0"),sQuery(id+"F0.wireOp",EDGE,"E4.7.0.1")])]});
            var Q27;
            Q27=makeQuery(id+"F1.opExtrude","SWEPT_EDGE",EDGE,{"disambiguationData":[OSD([sQuery(id+"F0.wireOp",EDGE,"E4.7.0.1"),sQuery(id+"F0.wireOp",EDGE,"E4.7.0.2")])]});
            var Q28;
            {var subQ0=sQuery(id+"F0.wireOp",EDGE,"E5.0.1.17");Q28=makeQuery(id+"F2.opFillet","BLEND_EDGE",EDGE,{"blendedFrom":[makeQuery(id+"F1.opExtrude","SWEPT_EDGE",EDGE,{"disambiguationData":[OSD([subQ0,sQuery(id+"F0.wireOp",EDGE,"E5.0.1.31")])]}),makeQuery(id+"F1.opExtrude","SWEPT_FACE",FACE,{"disambiguationData":[OSD([subQ0])]})],"blendedInto":[makeQuery(id+"F1.opExtrude","SWEPT_FACE",FACE,{"disambiguationData":[OSD([subQ0])]})]});}
            var Q29;
            Q29=makeQuery(id+"F1.opExtrude","SWEPT_EDGE",EDGE,{"disambiguationData":[OSD([sQuery(id+"F0.wireOp",EDGE,"E4.7.0.2"),sQuery(id+"F0.wireOp",EDGE,"E4.7.0.3")])]});
            var Q30;
            Q30=makeQuery(id+"F1.opExtrude","SWEPT_EDGE",EDGE,{"disambiguationData":[OSD([sQuery(id+"F0.wireOp",EDGE,"E4.7.0.3"),sQuery(id+"F0.wireOp",EDGE,"E4.8.0.0")])]});
            var Q31;
            Q31=makeQuery(id+"F1.opExtrude","SWEPT_EDGE",EDGE,{"disambiguationData":[OSD([sQuery(id+"F0.wireOp",EDGE,"E4.8.0.0"),sQuery(id+"F0.wireOp",EDGE,"E4.8.0.1")])]});
            var Q32;
            Q32=makeQuery(id+"F1.opExtrude","SWEPT_EDGE",EDGE,{"disambiguationData":[OSD([sQuery(id+"F0.wireOp",EDGE,"E4.8.0.1"),sQuery(id+"F0.wireOp",EDGE,"E4.8.0.2")])]});
            var Q33;
            Q33=makeQuery(id+"F1.opExtrude","SWEPT_EDGE",EDGE,{"disambiguationData":[OSD([sQuery(id+"F0.wireOp",EDGE,"E4.8.0.2"),sQuery(id+"F0.wireOp",EDGE,"E4.8.0.3")])]});
            var Q34;
            Q34=makeQuery(id+"F1.opExtrude","SWEPT_EDGE",EDGE,{"disambiguationData":[OSD([sQuery(id+"F0.wireOp",EDGE,"E4.8.0.3"),sQuery(id+"F0.wireOp",EDGE,"E4.9.0.0")])]});
            var Q35;
            Q35=makeQuery(id+"F1.opExtrude","SWEPT_EDGE",EDGE,{"disambiguationData":[OSD([sQuery(id+"F0.wireOp",EDGE,"E4.9.0.0"),sQuery(id+"F0.wireOp",EDGE,"E4.9.0.1")])]});
            var Q36;
            Q36=makeQuery(id+"F1.opExtrude","SWEPT_EDGE",EDGE,{"disambiguationData":[OSD([sQuery(id+"F0.wireOp",EDGE,"E4.9.0.1"),sQuery(id+"F0.wireOp",EDGE,"E4.9.0.2")])]});
            var Q37;
            Q37=makeQuery(id+"F1.opExtrude","SWEPT_EDGE",EDGE,{"disambiguationData":[OSD([sQuery(id+"F0.wireOp",EDGE,"E4.9.0.2"),sQuery(id+"F0.wireOp",EDGE,"E4.9.0.3")])]});
            var Q38;
            Q38=makeQuery(id+"F1.opExtrude","SWEPT_EDGE",EDGE,{"disambiguationData":[OSD([sQuery(id+"F0.wireOp",EDGE,"E4.9.0.3"),sQuery(id+"F0.wireOp",EDGE,"E4.10.0.0")])]});
            var Q39;
            Q39=makeQuery(id+"F1.opExtrude","SWEPT_EDGE",EDGE,{"disambiguationData":[OSD([sQuery(id+"F0.wireOp",EDGE,"E4.10.0.0"),sQuery(id+"F0.wireOp",EDGE,"E4.10.0.1")])]});
            var Q40;
            Q40=makeQuery(id+"F1.opExtrude","SWEPT_EDGE",EDGE,{"disambiguationData":[OSD([sQuery(id+"F0.wireOp",EDGE,"E4.10.0.1"),sQuery(id+"F0.wireOp",EDGE,"E4.10.0.2")])]});
            var Q41;
            Q41=makeQuery(id+"F1.opExtrude","SWEPT_EDGE",EDGE,{"disambiguationData":[OSD([sQuery(id+"F0.wireOp",EDGE,"E4.10.0.2"),sQuery(id+"F0.wireOp",EDGE,"E4.10.0.3")])]});
            var Q42;
            Q42=makeQuery(id+"F1.opExtrude","SWEPT_EDGE",EDGE,{"disambiguationData":[OSD([sQuery(id+"F0.wireOp",EDGE,"E4.10.0.3"),sQuery(id+"F0.wireOp",EDGE,"E4.11.0.0")])]});
            var Q43;
            Q43=makeQuery(id+"F1.opExtrude","SWEPT_EDGE",EDGE,{"disambiguationData":[OSD([sQuery(id+"F0.wireOp",EDGE,"E4.11.0.0"),sQuery(id+"F0.wireOp",EDGE,"E4.11.0.1")])]});
            var Q44;
            Q44=makeQuery(id+"F1.opExtrude","SWEPT_EDGE",EDGE,{"disambiguationData":[OSD([sQuery(id+"F0.wireOp",EDGE,"E4.11.0.1"),sQuery(id+"F0.wireOp",EDGE,"E4.11.0.2")])]});
            var Q45;
            Q45=makeQuery(id+"F1.opExtrude","SWEPT_EDGE",EDGE,{"disambiguationData":[OSD([sQuery(id+"F0.wireOp",EDGE,"E4.11.0.2"),sQuery(id+"F0.wireOp",EDGE,"E4.11.0.3")])]});
            var Q46;
            Q46=makeQuery(id+"F1.opExtrude","SWEPT_EDGE",EDGE,{"disambiguationData":[OSD([sQuery(id+"F0.wireOp",EDGE,"E4.11.0.3"),sQuery(id+"F0.wireOp",EDGE,"E4.12.0.0")])]});
            var Q47;
            Q47=makeQuery(id+"F1.opExtrude","SWEPT_EDGE",EDGE,{"disambiguationData":[OSD([sQuery(id+"F0.wireOp",EDGE,"E4.12.0.0"),sQuery(id+"F0.wireOp",EDGE,"E4.12.0.1")])]});
            var Q48;
            Q48=makeQuery(id+"F1.opExtrude","SWEPT_EDGE",EDGE,{"disambiguationData":[OSD([sQuery(id+"F0.wireOp",EDGE,"E4.12.0.1"),sQuery(id+"F0.wireOp",EDGE,"E4.12.0.2")])]});
            var Q49;
            Q49=makeQuery(id+"F1.opExtrude","SWEPT_EDGE",EDGE,{"disambiguationData":[OSD([sQuery(id+"F0.wireOp",EDGE,"E4.12.0.2"),sQuery(id+"F0.wireOp",EDGE,"E4.12.0.3")])]});
            var Q50;
            Q50=makeQuery(id+"F1.opExtrude","SWEPT_EDGE",EDGE,{"disambiguationData":[OSD([sQuery(id+"F0.wireOp",EDGE,"E4.12.0.3"),sQuery(id+"F0.wireOp",EDGE,"E4.13.0.0")])]});
            var Q51;
            Q51=makeQuery(id+"F1.opExtrude","SWEPT_EDGE",EDGE,{"disambiguationData":[OSD([sQuery(id+"F0.wireOp",EDGE,"E4.13.0.0"),sQuery(id+"F0.wireOp",EDGE,"E4.13.0.1")])]});
            var Q52;
            Q52=makeQuery(id+"F1.opExtrude","SWEPT_EDGE",EDGE,{"disambiguationData":[OSD([sQuery(id+"F0.wireOp",EDGE,"E4.13.0.1"),sQuery(id+"F0.wireOp",EDGE,"E4.13.0.2")])]});
            var Q53;
            Q53=makeQuery(id+"F1.opExtrude","SWEPT_EDGE",EDGE,{"disambiguationData":[OSD([sQuery(id+"F0.wireOp",EDGE,"E4.13.0.2"),sQuery(id+"F0.wireOp",EDGE,"E4.13.0.3")])]});
            var Q54;
            Q54=makeQuery(id+"F1.opExtrude","SWEPT_EDGE",EDGE,{"disambiguationData":[OSD([sQuery(id+"F0.wireOp",EDGE,"E4.13.0.3"),sQuery(id+"F0.wireOp",EDGE,"E4.14.0.0")])]});
            var Q55;
            Q55=makeQuery(id+"F1.opExtrude","SWEPT_EDGE",EDGE,{"disambiguationData":[OSD([sQuery(id+"F0.wireOp",EDGE,"E4.14.0.0"),sQuery(id+"F0.wireOp",EDGE,"E4.14.0.1")])]});
            var Q56;
            Q56=makeQuery(id+"F1.opExtrude","SWEPT_EDGE",EDGE,{"disambiguationData":[OSD([sQuery(id+"F0.wireOp",EDGE,"E4.14.0.1"),sQuery(id+"F0.wireOp",EDGE,"E4.14.0.2")])]});
            var Q57;
            Q57=makeQuery(id+"F1.opExtrude","SWEPT_EDGE",EDGE,{"disambiguationData":[OSD([sQuery(id+"F0.wireOp",EDGE,"E4.14.0.2"),sQuery(id+"F0.wireOp",EDGE,"E4.14.0.3")])]});
            fillet(context, id + "F3", {"entities" : qUnion([Q0, Q1, Q2, Q3, Q4, Q5, Q6, Q7, Q8, Q9, Q10, Q11, Q12, Q13, Q14, Q15, Q16, Q17, Q18, Q19, Q20, Q21, Q22, Q23, Q24, Q25, Q26, Q27, Q28, Q29, Q30, Q31, Q32, Q33, Q34, Q35, Q36, Q37, Q38, Q39, Q40, Q41, Q42, Q43, Q44, Q45, Q46, Q47, Q48, Q49, Q50, Q51, Q52, Q53, Q54, Q55, Q56, Q57]), "radius" : 12.7 * mm, "tangentPropagation" : true, "allowEdgeOverflow" : false});
        }
    });
